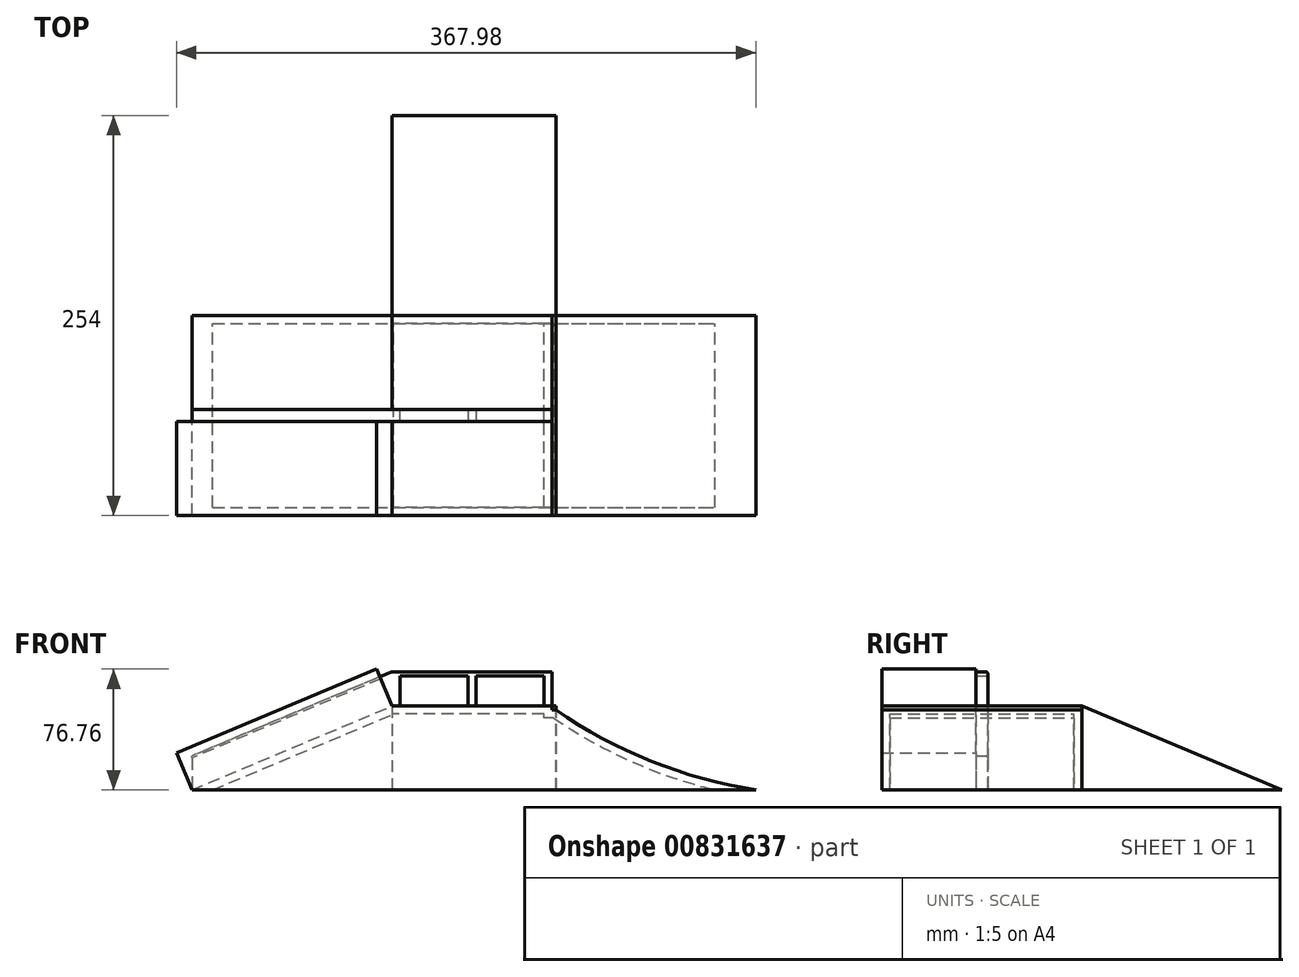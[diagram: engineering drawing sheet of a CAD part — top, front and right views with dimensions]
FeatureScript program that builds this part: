
annotation { "Feature Type Name" : "Feature", "Feature Type Description" : "" }
export const myFeature = defineFeature(function(context is Context, id is Id, definition is map)
    precondition{}
    {
        {
            var Q0;
            Q0=qCreatedBy(makeId("Front.planeOp"),FACE);
            var sketch = newSketch(context, id + "F0", { "sketchPlane" : qUnion([Q0])});
            skLineSegment(sketch, "E0.bottom", {"start": v(0, 0) * mm, "end": v(127, 0) * mm});
            skLineSegment(sketch, "E0.left", {"start": v(0, 0) * mm, "end": v(0, 50.8) * mm});
            skArc(sketch, "E1", {"start": v(0, 50.8) * mm, "mid": v(60.61, 18.18) * mm, "end": v(127, 0) * mm});
            skLineSegment(sketch, "E2.bottom", {"start": v(0, 0) * mm, "end": v(-2.54, 0) * mm});
            skLineSegment(sketch, "E2.top", {"start": v(0, 50.8) * mm, "end": v(-2.54, 50.8) * mm});
            skLineSegment(sketch, "E2.right", {"start": v(-2.54, 0) * mm, "end": v(-2.54, 50.8) * mm});
            skLineSegment(sketch, "E3.bottom", {"start": v(-2.54, 0) * mm, "end": v(-104.14, 0) * mm});
            skLineSegment(sketch, "E3.top", {"start": v(-2.54, 53.34) * mm, "end": v(-104.14, 53.34) * mm});
            skLineSegment(sketch, "E3.left", {"start": v(-2.54, 0) * mm, "end": v(-2.54, 53.34) * mm});
            skLineSegment(sketch, "E3.right", {"start": v(-104.14, 0) * mm, "end": v(-104.14, 53.34) * mm});
            skCircle(sketch, "E4", {"center": v(-1.27, 52.07) * mm, "radius": 1.27 * mm});
            skPoint(sketch, "E4.centerSnap0", {"position": v(-1.27, 50.8) * mm});
            skLineSegment(sketch, "E5", {"start": v(-104.14, 0) * mm, "end": v(-231.14, 0) * mm});
            skLineSegment(sketch, "E6", {"start": v(-231.14, 0) * mm, "end": v(-104.14, 53.34) * mm});
            skSolve(sketch);
        }
        {
            var Q0;
            Q0=makeQuery(id+"F0.imprint","IMPRINT",FACE,{"disambiguationData":[TD([[makeQuery(id+"F0.imprint","IMPRINT",EDGE,{"derivedFrom":sQuery(id+"F0.wireOp",EDGE,"E0.bottom")}),1.0]])]});
            var Q1;
            Q1=makeQuery(id+"F0.imprint","IMPRINT",FACE,{"disambiguationData":[TD([[makeQuery(id+"F0.imprint","IMPRINT",EDGE,{"derivedFrom":sQuery(id+"F0.wireOp",EDGE,"gSf4ow2M-3nON-57kk-JyT3-ZSVy4p9OPfto.bottom")}),-1.0]])]});
            var Q2;
            {var subQ3=sQuery(id+"F0.wireOp",EDGE,"E3.bottom");Q2=makeQuery(id+"F0.imprint","IMPRINT",FACE,{"disambiguationData":[TD([[makeQuery(id+"F0.imprint","IMPRINT",EDGE,{"derivedFrom":subQ3}),-1.0]])]});}
            var Q3;
            {var subQ5=sQuery(id+"F0.wireOp",EDGE,"E2.bottom");Q3=makeQuery(id+"F0.imprint","IMPRINT",FACE,{"disambiguationData":[TD([[makeQuery(id+"F0.imprint","IMPRINT",EDGE,{"derivedFrom":subQ5}),-1.0]])]});}
            var Q4;
            {var subQ0=sQuery(id+"F0.wireOp",EDGE,"E4");var subQ1=makeQuery(id+"F0.imprint","INTERSECT",VERTEX,{"derivedFrom":[sQuery(id+"F0.wireOp",EDGE,"E2.top"),subQ0]});Q4=makeQuery(id+"F0.imprint","IMPRINT",FACE,{"disambiguationData":[TD([[makeQuery(id+"F0.imprint","IMPRINT",EDGE,{"disambiguationData":[TD([[subQ1,1.0]])],"derivedFrom":subQ0}),1.0]])]});}
            var Q5;
            Q5=makeQuery(id+"F0.imprint","IMPRINT",FACE,{"disambiguationData":[TD([[makeQuery(id+"F0.imprint","IMPRINT",EDGE,{"derivedFrom":sQuery(id+"F0.wireOp",EDGE,"E3.right")}),1.0]])]});
            extrude(context, id + "F1", {"entities" : qUnion([Q0, Q1, Q2, Q3, Q4, Q5]), "depth" : 127 * mm});
        }
        {
            var Q0;
            Q0=makeQuery(id+"F1.opExtrude","SWEPT_FACE",FACE,{"disambiguationData":[OSD([sQuery(id+"F0.wireOp",EDGE,"E3.top")])]});
            var sketch = newSketch(context, id + "F2", { "sketchPlane" : qUnion([Q0])});
            skLineSegment(sketch, "E7.bottom", {"start": v(-104.14, -67.31) * mm, "end": v(-99.06, -67.31) * mm});
            skLineSegment(sketch, "E7.top", {"start": v(-104.14, -59.7) * mm, "end": v(-99.06, -59.7) * mm});
            skLineSegment(sketch, "E7.left", {"start": v(-104.14, -67.31) * mm, "end": v(-104.14, -59.7) * mm});
            skLineSegment(sketch, "E7.right", {"start": v(-99.06, -67.31) * mm, "end": v(-99.06, -59.7) * mm});
            skLineSegment(sketch, "E8.bottom", {"start": v(-2.54, -67.3) * mm, "end": v(-7.62, -67.3) * mm});
            skLineSegment(sketch, "E8.top", {"start": v(-2.54, -59.7) * mm, "end": v(-7.62, -59.7) * mm});
            skLineSegment(sketch, "E8.left", {"start": v(-2.54, -67.3) * mm, "end": v(-2.54, -59.7) * mm});
            skLineSegment(sketch, "E8.right", {"start": v(-7.62, -67.3) * mm, "end": v(-7.62, -59.7) * mm});
            skLineSegment(sketch, "E9.bottom", {"start": v(-55.88, -59.7) * mm, "end": v(-50.8, -59.7) * mm});
            skLineSegment(sketch, "E9.top", {"start": v(-55.88, -67.31) * mm, "end": v(-50.8, -67.31) * mm});
            skLineSegment(sketch, "E9.left", {"start": v(-55.88, -59.7) * mm, "end": v(-55.88, -67.31) * mm});
            skLineSegment(sketch, "E9.right", {"start": v(-50.8, -59.7) * mm, "end": v(-50.8, -67.31) * mm});
            skSolve(sketch);
        }
        {
            var Q0;
            Q0=qSketchRegion(id+"F2",true);
            extrude(context, id + "F3", {"entities" : qUnion([Q0]), "operationType" : NewBodyOperationType.ADD, "depth" : 19.05 * mm});
        }
        {
            var Q0;
            Q0=makeQuery(id+"F3.boolean.opBoolean","MERGE",FACE,{"derivedFrom":[makeQuery(id+"F1.opExtrude","SWEPT_FACE",FACE,{"disambiguationData":[OSD([sQuery(id+"F0.wireOp",EDGE,"E3.left")])]}),makeQuery(id+"F3.opExtrude","SWEPT_FACE",FACE,{"disambiguationData":[OSD([sQuery(id+"F2.wireOp",EDGE,"E8.left")])]})]});
            var sketch = newSketch(context, id + "F4", { "sketchPlane" : qUnion([Q0])});
            skLineSegment(sketch, "E10.bottom", {"start": v(-67.3, 72.4) * mm, "end": v(-59.7, 72.4) * mm});
            skLineSegment(sketch, "E10.top", {"start": v(-67.3, 74.93) * mm, "end": v(-59.7, 74.93) * mm});
            skLineSegment(sketch, "E10.left", {"start": v(-67.3, 72.4) * mm, "end": v(-67.3, 74.93) * mm});
            skLineSegment(sketch, "E10.right", {"start": v(-59.7, 72.4) * mm, "end": v(-59.7, 74.93) * mm});
            skSolve(sketch);
        }
        {
            var Q0;
            Q0=makeQuery(id+"F4.imprint","IMPRINT",FACE,{"disambiguationData":[TD([[makeQuery(id+"F4.imprint","IMPRINT",EDGE,{"derivedFrom":sQuery(id+"F4.wireOp",EDGE,"E10.bottom")}),1.0]])]});
            extrude(context, id + "F5", {"entities" : qUnion([Q0]), "operationType" : NewBodyOperationType.ADD, "oppositeDirection" : true, "depth" : 101.6 * mm});
        }
        {
            var Q0;
            Q0=makeQuery(id+"F1.opExtrude","SWEPT_FACE",FACE,{"disambiguationData":[OSD([sQuery(id+"F0.wireOp",EDGE,"E0.bottom"),sQuery(id+"F0.wireOp",EDGE,"E2.bottom"),sQuery(id+"F0.wireOp",EDGE,"E3.bottom"),sQuery(id+"F0.wireOp",EDGE,"E5")])]});
            shell(context, id + "F6", {"entities" : qUnion([Q0]), "thickness" : 5.08 * mm});
        }
        {
            var Q0;
            Q0=makeQuery(id+"F5.boolean.opBoolean","MERGE",FACE,{"derivedFrom":[makeQuery(id+"F3.opExtrude","SWEPT_FACE",FACE,{"disambiguationData":[OSD([sQuery(id+"F2.wireOp",EDGE,"E7.top")])]}),makeQuery(id+"F3.opExtrude","SWEPT_FACE",FACE,{"disambiguationData":[OSD([sQuery(id+"F2.wireOp",EDGE,"E8.top")])]}),makeQuery(id+"F3.opExtrude","SWEPT_FACE",FACE,{"disambiguationData":[OSD([sQuery(id+"F2.wireOp",EDGE,"E9.bottom")])]}),makeQuery(id+"F5.opExtrude","SWEPT_FACE",FACE,{"disambiguationData":[OSD([sQuery(id+"F4.wireOp",EDGE,"E10.right")])]})]});
            var sketch = newSketch(context, id + "F7", { "sketchPlane" : qUnion([Q0])});
            skLineSegment(sketch, "E11", {"start": v(104.14, 74.93) * mm, "end": v(231.14, 21.59) * mm});
            skLineSegment(sketch, "E12", {"start": v(231.14, 21.59) * mm, "end": v(231.14, 0) * mm});
            skLineSegment(sketch, "E13", {"start": v(231.14, 0) * mm, "end": v(104.14, 53.34) * mm});
            skLineSegment(sketch, "E14", {"start": v(104.14, 74.93) * mm, "end": v(104.14, 53.34) * mm});
            skSolve(sketch);
        }
        {
            var Q0;
            Q0=qSketchRegion(id+"F7",true);
            extrude(context, id + "F8", {"entities" : qUnion([Q0]), "operationType" : NewBodyOperationType.ADD, "oppositeDirection" : true, "depth" : 7.62 * mm});
        }
        {
            var Q0;
            Q0=qCreatedBy(makeId("Right.planeOp"),FACE);
            var sketch = newSketch(context, id + "F9", { "sketchPlane" : qUnion([Q0])});
            skLineSegment(sketch, "E15", {"start": v(0, 53.34) * mm, "end": v(127, 0) * mm});
            skLineSegment(sketch, "E16", {"start": v(127, 0) * mm, "end": v(0, 0) * mm});
            skLineSegment(sketch, "E17", {"start": v(0, 0) * mm, "end": v(0, 53.34) * mm});
            skSolve(sketch);
        }
        {
            var Q0;
            Q0=makeQuery(id+"F9.imprint","IMPRINT",FACE,{"disambiguationData":[TD([[makeQuery(id+"F9.imprint","IMPRINT",EDGE,{"derivedFrom":sQuery(id+"F9.wireOp",EDGE,"E15")}),-1.0]])]});
            extrude(context, id + "F10", {"entities" : qUnion([Q0]), "oppositeDirection" : true, "depth" : 104.14 * mm});
        }
        {
            var Q0;
            Q0=makeQuery(id+"F5.opExtrude","SWEPT_EDGE",EDGE,{"disambiguationData":[OSD([sQuery(id+"F4.wireOp",EDGE,"E10.top"),sQuery(id+"F4.wireOp",EDGE,"E10.left")])]});
            var Q1;
            Q1=makeQuery(id+"F8.opExtrude","CAP_EDGE",EDGE,{"disambiguationData":[OSD([sQuery(id+"F7.wireOp",EDGE,"E11")])],"isStart":false});
            var Q2;
            {var subQ0=sQuery(id+"F4.wireOp",EDGE,"E10.top");Q2=makeQuery(id+"F8.boolean.opBoolean","MERGE",EDGE,{"derivedFrom":[makeQuery(id+"F5.opExtrude","CAP_EDGE",EDGE,{"disambiguationData":[OSD([subQ0])],"isStart":false}),makeQuery(id+"F8.opExtrude","SWEPT_EDGE",EDGE,{"disambiguationData":[OSD([subQ0,sQuery(id+"F4.wireOp",EDGE,"E10.right"),sQuery(id+"F7.wireOp",EDGE,"E11"),sQuery(id+"F7.wireOp",EDGE,"E14")])]})]});}
            var Q3;
            Q3=makeQuery(id+"F8.opExtrude","CAP_EDGE",EDGE,{"disambiguationData":[OSD([sQuery(id+"F7.wireOp",EDGE,"E11")])],"isStart":true});
            var Q4;
            Q4=makeQuery(id+"F5.opExtrude","SWEPT_EDGE",EDGE,{"disambiguationData":[OSD([sQuery(id+"F4.wireOp",EDGE,"E10.top"),sQuery(id+"F4.wireOp",EDGE,"E10.right")])]});
            fillet(context, id + "F11", {"entities" : qUnion([Q0, Q1, Q2, Q3, Q4]), "radius" : 1.27 * mm, "tangentPropagation" : true, "allowEdgeOverflow" : false});
        }
        {
            var Q0;
            {var subQ0=sQuery(id+"F0.wireOp",EDGE,"E6");Q0=makeQuery(id+"F8.boolean.opBoolean","SPLIT",FACE,{"disambiguationData":[TD([makeQuery(id+"F3.opExtrude","SWEPT_FACE",FACE,{"disambiguationData":[OSD([sQuery(id+"F2.wireOp",EDGE,"E7.bottom")])]})])],"derivedFrom":makeQuery(id+"F1.opExtrude","SWEPT_FACE",FACE,{"disambiguationData":[OSD([subQ0])]})});}
            extrude(context, id + "F12", {"entities" : qUnion([Q0]), "operationType" : NewBodyOperationType.ADD, "depth" : 25.4 * mm, "offsetDistance" : 25.4 * mm});
        }
    });
